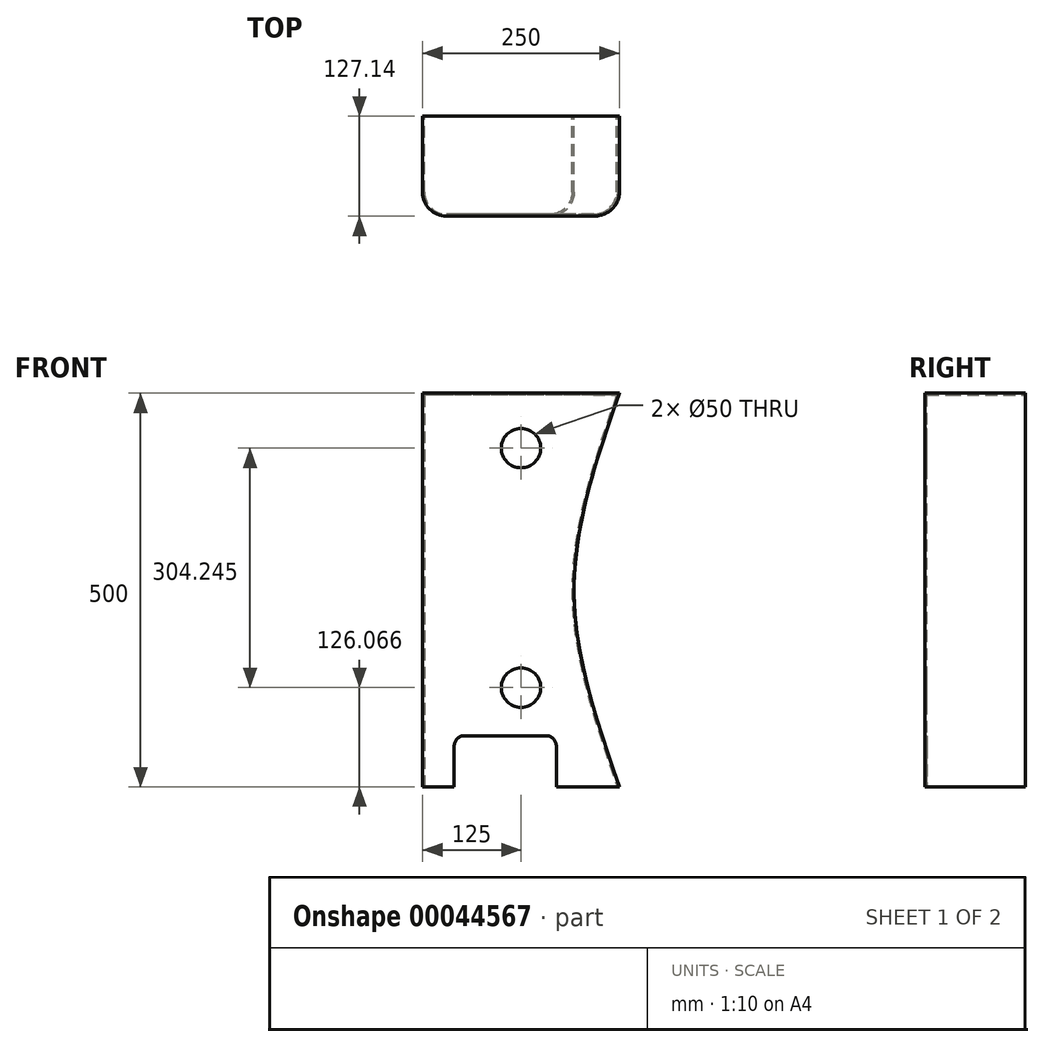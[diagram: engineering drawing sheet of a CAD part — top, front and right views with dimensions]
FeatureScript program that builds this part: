
annotation { "Feature Type Name" : "Feature", "Feature Type Description" : "" }
export const myFeature = defineFeature(function(context is Context, id is Id, definition is map)
    precondition{}
    {
        {
            var Q0;
            Q0=qCreatedBy(makeId("Front.planeOp"),FACE);
            var sketch = newSketch(context, id + "F7", { "sketchPlane" : qUnion([Q0])});
            skLineSegment(sketch, "E0.rect.bottom", {"start": v(125, 250) * mm, "end": v(-125, 250) * mm});
            skLineSegment(sketch, "E0.rect.top", {"start": v(125, -250) * mm, "end": v(-125, -250) * mm});
            skLineSegment(sketch, "E0.rect.left", {"start": v(125, 250) * mm, "end": v(125, -250) * mm});
            skLineSegment(sketch, "E0.rect.right", {"start": v(-125, 250) * mm, "end": v(-125, -250) * mm});
            skPoint(sketch, "E0.rect.middle", {"position": v(0, 0) * mm});
            skFitSpline(sketch, "E1", {"points": [v(125, 250) * mm, v(67.33, 0) * mm, v(125, -250) * mm], "startDerivative": vector(-173, -500) * mm, "endDerivative": vector(173, -500) * mm});
            skSolve(sketch);
        }
        {
            var Q0;
            Q0=makeQuery(id+"F7.imprint","IMPRINT",FACE,{"disambiguationData":[TD([[makeQuery(id+"F7.imprint","IMPRINT",EDGE,{"derivedFrom":sQuery(id+"F7.wireOp",EDGE,"E0.rect.bottom")}),1.0]])]});
            extrude(context, id + "F0", {"entities" : qUnion([Q0]), "depth" : 127.14 * mm});
        }
        {
            var Q0;
            Q0=makeQuery(id+"F0.opExtrude","CAP_EDGE",EDGE,{"disambiguationData":[OSD([sQuery(id+"F7.wireOp",EDGE,"E1")])],"isStart":false});
            var Q1;
            Q1=makeQuery(id+"F0.opExtrude","CAP_EDGE",EDGE,{"disambiguationData":[OSD([sQuery(id+"F7.wireOp",EDGE,"E0.rect.right")])],"isStart":false});
            fillet(context, id + "F8", {"entities" : qUnion([Q0, Q1]), "radius" : 30.5 * mm, "tangentPropagation" : true, "allowEdgeOverflow" : false});
        }
        {
            var Q0;
            Q0=makeQuery(id+"F0.opExtrude","CAP_FACE",FACE,{"disambiguationData":[OSD([sQuery(id+"F7.wireOp",EDGE,"E0.rect.bottom"),sQuery(id+"F7.wireOp",EDGE,"E0.rect.top"),sQuery(id+"F7.wireOp",EDGE,"E0.rect.right"),sQuery(id+"F7.wireOp",EDGE,"E1")])],"isStart":true});
            var sketch = newSketch(context, id + "F9", { "sketchPlane" : qUnion([Q0])});
            skLineSegment(sketch, "E2.bottom", {"start": v(85, -250) * mm, "end": v(-45, -250) * mm});
            skLineSegment(sketch, "E2.top", {"start": v(85, -185) * mm, "end": v(-45, -185) * mm});
            skLineSegment(sketch, "E2.left", {"start": v(85, -250) * mm, "end": v(85, -185) * mm});
            skLineSegment(sketch, "E2.right", {"start": v(-45, -250) * mm, "end": v(-45, -185) * mm});
            skSolve(sketch);
        }
        {
            var Q0;
            Q0=makeQuery(id+"F9.imprint","IMPRINT",FACE,{"disambiguationData":[TD([[makeQuery(id+"F9.imprint","IMPRINT",EDGE,{"derivedFrom":sQuery(id+"F9.wireOp",EDGE,"E2.bottom")}),1.0]])]});
            extrude(context, id + "F1", {"entities" : qUnion([Q0]), "operationType" : NewBodyOperationType.REMOVE, "oppositeDirection" : true, "depth" : 404.41 * mm});
        }
        {
            var Q0;
            Q0=makeQuery(id+"F1.boolean.opBoolean","COPY",EDGE,{"derivedFrom":makeQuery(id+"F1.opExtrude","SWEPT_EDGE",EDGE,{"disambiguationData":[OSD([sQuery(id+"F9.wireOp",EDGE,"E2.top"),sQuery(id+"F9.wireOp",EDGE,"E2.right")])]})});
            var Q1;
            Q1=makeQuery(id+"F1.boolean.opBoolean","COPY",EDGE,{"derivedFrom":makeQuery(id+"F1.opExtrude","SWEPT_EDGE",EDGE,{"disambiguationData":[OSD([sQuery(id+"F9.wireOp",EDGE,"E2.top"),sQuery(id+"F9.wireOp",EDGE,"E2.left")])]})});
            fillet(context, id + "F2", {"entities" : qUnion([Q0, Q1]), "radius" : 13.6 * mm, "tangentPropagation" : true, "allowEdgeOverflow" : false});
        }
        {
            var Q0;
            Q0=makeQuery(id+"F0.opExtrude","CAP_FACE",FACE,{"disambiguationData":[OSD([sQuery(id+"F7.wireOp",EDGE,"E0.rect.bottom"),sQuery(id+"F7.wireOp",EDGE,"E0.rect.top"),sQuery(id+"F7.wireOp",EDGE,"E0.rect.right"),sQuery(id+"F7.wireOp",EDGE,"E1")])],"isStart":true});
            var Q1;
            Q1=makeQuery(id+"F1.boolean.opBoolean","COPY",FACE,{"derivedFrom":makeQuery(id+"F1.opExtrude","SWEPT_FACE",FACE,{"disambiguationData":[OSD([sQuery(id+"F9.wireOp",EDGE,"E2.top")])]})});
            var Q2;
            Q2=makeQuery(id+"F2.opFillet","BLEND_FACE",FACE,{"disambiguationData":[OSD([sQuery(id+"F9.wireOp",EDGE,"E2.top"),sQuery(id+"F9.wireOp",EDGE,"E2.left")])]});
            var Q3;
            Q3=makeQuery(id+"F2.opFillet","BLEND_FACE",FACE,{"disambiguationData":[OSD([sQuery(id+"F9.wireOp",EDGE,"E2.top"),sQuery(id+"F9.wireOp",EDGE,"E2.right")])]});
            var Q4;
            {var subQ0=sQuery(id+"F7.wireOp",EDGE,"E0.rect.top");var subQ3=sQuery(id+"F7.wireOp",EDGE,"E1");Q4=makeQuery(id+"F1.boolean.opBoolean","SPLIT",FACE,{"disambiguationData":[TD([makeQuery(id+"F0.opExtrude","SWEPT_FACE",FACE,{"disambiguationData":[OSD([subQ3])]})])],"derivedFrom":makeQuery(id+"F0.opExtrude","SWEPT_FACE",FACE,{"disambiguationData":[OSD([subQ0])]})});}
            var Q5;
            {var subQ0=sQuery(id+"F7.wireOp",EDGE,"E0.rect.top");var subQ2=sQuery(id+"F7.wireOp",EDGE,"E0.rect.right");Q5=makeQuery(id+"F1.boolean.opBoolean","SPLIT",FACE,{"disambiguationData":[TD([makeQuery(id+"F0.opExtrude","SWEPT_FACE",FACE,{"disambiguationData":[OSD([subQ2])]})])],"derivedFrom":makeQuery(id+"F0.opExtrude","SWEPT_FACE",FACE,{"disambiguationData":[OSD([subQ0])]})});}
            var Q6;
            Q6=makeQuery(id+"F1.boolean.opBoolean","COPY",FACE,{"derivedFrom":makeQuery(id+"F1.opExtrude","SWEPT_FACE",FACE,{"disambiguationData":[OSD([sQuery(id+"F9.wireOp",EDGE,"E2.left")])]})});
            var Q7;
            Q7=makeQuery(id+"F1.boolean.opBoolean","COPY",FACE,{"derivedFrom":makeQuery(id+"F1.opExtrude","SWEPT_FACE",FACE,{"disambiguationData":[OSD([sQuery(id+"F9.wireOp",EDGE,"E2.right")])]})});
            shell(context, id + "F3", {"entities" : qUnion([Q0, Q1, Q2, Q3, Q4, Q5, Q6, Q7]), "thickness" : 2.5 * mm});
        }
        {
            var Q0;
            Q0=makeQuery(id+"F0.opExtrude","CAP_FACE",FACE,{"disambiguationData":[OSD([sQuery(id+"F7.wireOp",EDGE,"E0.rect.bottom"),sQuery(id+"F7.wireOp",EDGE,"E0.rect.top"),sQuery(id+"F7.wireOp",EDGE,"E0.rect.right"),sQuery(id+"F7.wireOp",EDGE,"E1")])],"isStart":false});
            var sketch = newSketch(context, id + "F4", { "sketchPlane" : qUnion([Q0])});
            skPoint(sketch, "E3", {"position": v(0, 180.31) * mm});
            skPoint(sketch, "E4", {"position": v(0, -123.93) * mm});
            skSolve(sketch);
        }
        {
            var Q0;
            Q0=sQuery(id+"F4.wireOp",VERTEX,"E3");
            var Q1;
            Q1=sQuery(id+"F4.wireOp",VERTEX,"E4");
            var Q2;
            Q2=makeQuery(id+"F0.opExtrude","SWEPT_BODY",BODY,{"disambiguationData":[OSD([sQuery(id+"F7.wireOp",EDGE,"E0.rect.bottom"),sQuery(id+"F7.wireOp",EDGE,"E0.rect.top"),sQuery(id+"F7.wireOp",EDGE,"E0.rect.right"),sQuery(id+"F7.wireOp",EDGE,"E1")])]});
            hole(context, id + "F5", {"style" : HoleStyle.SIMPLE, "holeDiameter" : 50 * mm, "endStyle" : HoleEndStyle.THROUGH, "locations" : qUnion([Q0, Q1]), "scope" : qUnion([Q2])});
        }
    });
